# Revit family: AFX-Bailey-Flush_Mount-1
name_source: partatom
category: Lighting Fixtures
units: mm (PartAtom-declared; Revit-internal decimal feet)

## family parameters
Cut with Voids When Loaded = No
Host = Face
Light Source = Yes
Part Type = Normal
Room Calculation Point = No
Round Connector Dimension = Use Diameter
Shared = No

## types (2) — shared parameters
Apparent Load = 0 VA
Assembly Code = D5020200
Body Finish = AFX - Paint Finish Black
Color Filter = 16777215
Colour Rendering Index = 90
Default Elevation = 48"
Depth = 4"
Diffuser Finish = AFX - Acrylic
Dimming Lamp Color Temperature Shift = <None>
Emit Shape Visible in Rendering = Yes
Keynote = 12500
Manufacturer = AFX Inc
Power Factor = 1
Product Documentation Link = https://www.afxinc.com
Revit Model Built By = https://www.servex-us.com
Sustainability = https://lamprecycle.org
Tilt Angle = 90.00°
Type Comments = Bailey
URL = https://www.afxinc.com
Voltage = 120 V

## per-type parameters (varying)
| type | Description | Diameter | Emit from Circle Diameter | L | Photometric Web File | Wattage Comments |
| BAYF24LAJUDBK | LED Flush Mount - 24"Dia x 4"D | 24" | 23 1/4" | 12" | BAYF24LAJUDxx_3000K_IES.IES | 35w |
| BAYF30LAJUDBK | LED Flush Mount - 30"Dia x 4"D | 30" | 29 1/4" | 15" | BAYF30LAJUDBK_3000K IES.IES | 45w |

note: column(s) folded — value = type name in every type: Model

## geometry (parser evidence)
native form markers: Sweep x1
no freeform markers — native parametric forms only
